# Revit family: Bath-Drain-KOHLER-K-18355T_1
name_source: partatom
category: Plumbing Fixtures
revit_build: Autodesk Revit 2017 (Build: 20160225_1515(x64)
units: mm (PartAtom-declared; Revit-internal decimal feet)

## family parameters
Cut with Voids When Loaded = No
Host = Face
OmniClass Number = 23.31.15.17.23
OmniClass Title = Bathtub Drains
Part Type = Normal
Room Calculation Point = No
Round Connector Dimension = Use Diameter
Shared = No

## types (1)
- CP - Polished Chrome
    ADA Compliant = No
    Assembly Code = C1030200
    CW Connection = No
    Cold Water Inlet = Cold Water Inlet
    Date Modified = 03/12/2021
    Default Elevation = 0"
    Description = Bathtub drain (flexible hose)
    Finish = Kohler-Metal-CP-Polished_Chrome
    HW Connection = No
    Height = 23 9/16"
    Hot Water Inlet = Hot Water Inlet
    Length = 18 3/16"
    Manufacturer = KOHLER Co.
    Master Format 2014 = 22 41 19
    Master Format 2014 Name = Residential Bathtubs
    Material = Brass Construction
    Model = K-18355T-CP
    Product Documentation Link = https://files.kohler.com.cn
    Product Page URL = https://www.kohler.com.cn
    Type = 1
    URL = http://www.kohler.com.cn
    Vent Connection = No
    Waste Connection = Yes
    Waste Water Outlet = Waste Water Outlet
    WaterSense Certified = No
    Width = 9 1/4"

## geometry (parser evidence)
native form markers: Sweep x4
no freeform markers — native parametric forms only
